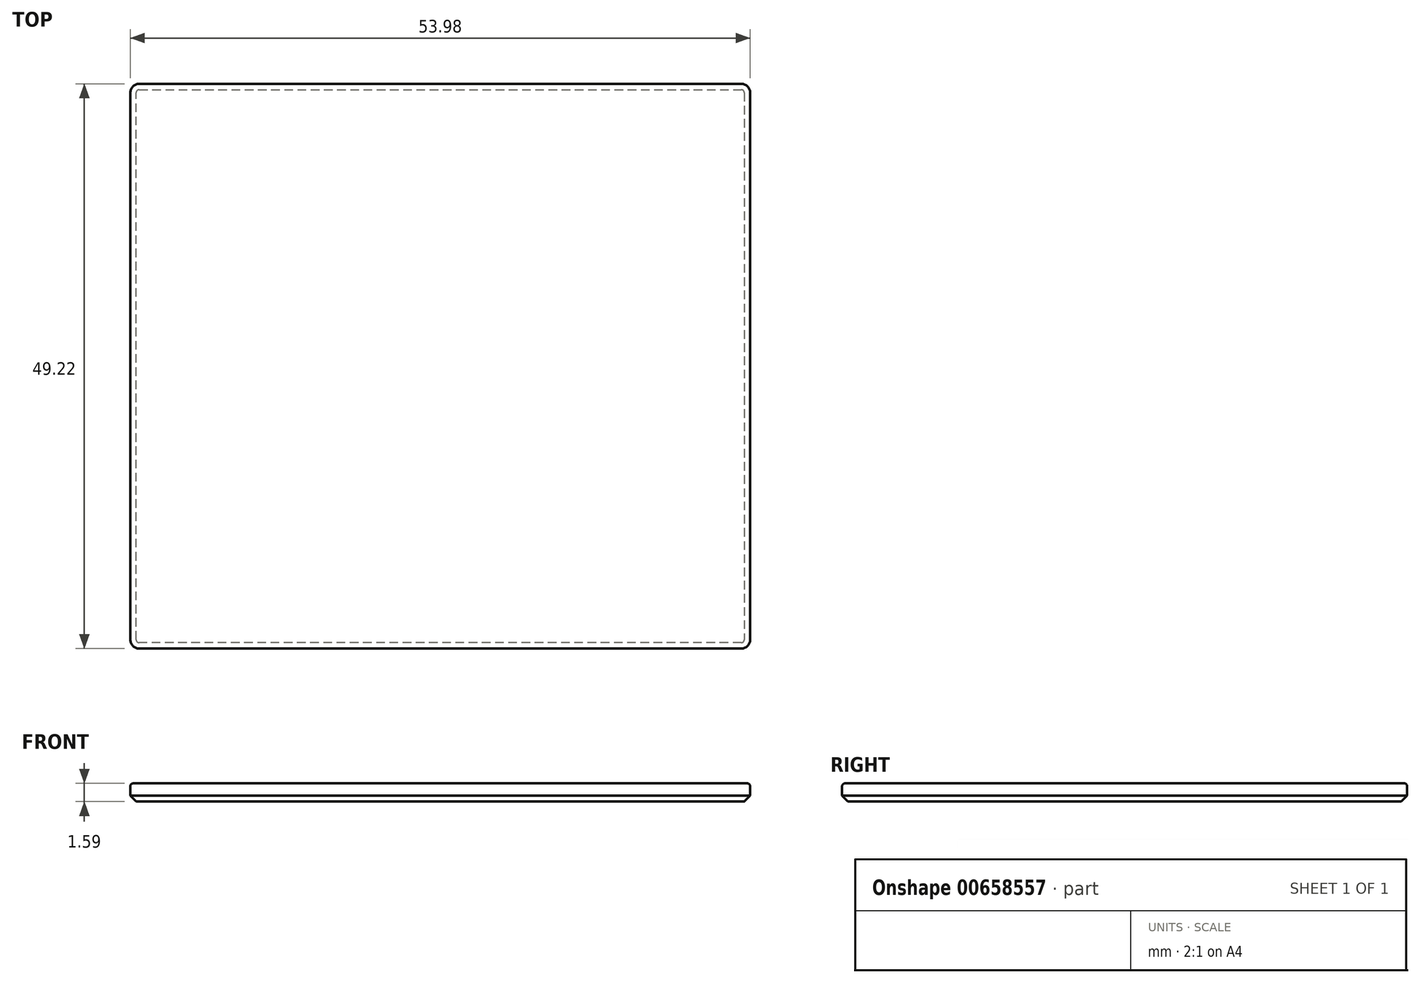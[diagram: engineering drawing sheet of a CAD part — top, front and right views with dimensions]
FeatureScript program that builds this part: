
annotation { "Feature Type Name" : "Feature", "Feature Type Description" : "" }
export const myFeature = defineFeature(function(context is Context, id is Id, definition is map)
    precondition{}
    {
        {
            var Q0;
            Q0=qCreatedBy(makeId("Top.planeOp"),FACE);
            var sketch = newSketch(context, id + "F0", { "sketchPlane" : qUnion([Q0])});
            skLineSegment(sketch, "E0.bottom", {"start": v(-26.99, 33.34) * mm, "end": v(26.99, 33.34) * mm});
            skLineSegment(sketch, "E0.top", {"start": v(-26.99, -15.88) * mm, "end": v(26.99, -15.88) * mm});
            skLineSegment(sketch, "E0.left", {"start": v(-26.99, 33.34) * mm, "end": v(-26.99, -15.88) * mm});
            skLineSegment(sketch, "E0.right", {"start": v(26.99, 33.34) * mm, "end": v(26.99, -15.87) * mm});
            skSolve(sketch);
        }
        {
            var Q0;
            Q0=qSketchRegion(id+"F0",true);
            extrude(context, id + "F1", {"entities" : qUnion([Q0]), "depth" : 1.59 * mm, "offsetDistance" : 25.4 * mm});
        }
        {
            var Q0;
            Q0=makeQuery(id+"F1.opExtrude","SWEPT_EDGE",EDGE,{"disambiguationData":[OSD([sQuery(id+"F0.wireOp",EDGE,"E0.top"),sQuery(id+"F0.wireOp",EDGE,"E0.left")])]});
            var Q1;
            Q1=makeQuery(id+"F1.opExtrude","SWEPT_EDGE",EDGE,{"disambiguationData":[OSD([sQuery(id+"F0.wireOp",EDGE,"E0.bottom"),sQuery(id+"F0.wireOp",EDGE,"E0.left")])]});
            var Q2;
            Q2=makeQuery(id+"F1.opExtrude","SWEPT_EDGE",EDGE,{"disambiguationData":[OSD([sQuery(id+"F0.wireOp",EDGE,"E0.bottom"),sQuery(id+"F0.wireOp",EDGE,"E0.right")])]});
            var Q3;
            Q3=makeQuery(id+"F1.opExtrude","SWEPT_EDGE",EDGE,{"disambiguationData":[OSD([sQuery(id+"F0.wireOp",EDGE,"E0.top"),sQuery(id+"F0.wireOp",EDGE,"E0.right")])]});
            fillet(context, id + "F3", {"entities" : qUnion([Q0, Q1, Q2, Q3]), "radius" : 0.76 * mm, "tangentPropagation" : true, "allowEdgeOverflow" : false});
        }
        {
            var Q0;
            Q0=makeQuery(id+"F1.opExtrude","CAP_EDGE",EDGE,{"disambiguationData":[OSD([sQuery(id+"F0.wireOp",EDGE,"E0.right")])],"isStart":false});
            fillet(context, id + "F4", {"entities" : qUnion([Q0]), "radius" : 0.25 * mm, "tangentPropagation" : true, "allowEdgeOverflow" : false});
        }
        {
            var Q0;
            Q0=makeQuery(id+"F1.opExtrude","CAP_EDGE",EDGE,{"disambiguationData":[OSD([sQuery(id+"F0.wireOp",EDGE,"E0.right")])],"isStart":true});
            chamfer(context, id + "F5", {"entities" : qUnion([Q0]), "width" : 0.5 * mm, "tangentPropagation" : true});
        }
    });
